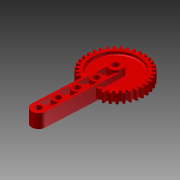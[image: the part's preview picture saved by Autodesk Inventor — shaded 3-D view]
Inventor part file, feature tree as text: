
AUTODESK INVENTOR PART (.ipt)
format: ipt  version: 2013 (Build 170138000, 138)  size: 1,695,232 bytes
history: native  units: mm (DEFAULTED — no unit token found)
features: plane x2, imported_body x1
ambient origin geometry x8: Origin, YZ Plane, XZ Plane, XY Plane, X Axis, Y Axis, Z Axis, Center Point
bodies: Solid1 (feature_tree)
feature tree (3):
  imported_body  "Base1"
  plane  "Work Plane1"
  plane  "Work Plane2"
